# Revit family: Kessel 27611 en
name_source: partatom
category: Pipe Accessories
revit_build: Autodesk Revit Architecture 2014 (Build: 20130308_1515(x64)
units: mm (PartAtom-declared; Revit-internal decimal feet)

## types (1)
- Kessel 27611 en
    <1.010.00.2> Number of the part of the guideline = 38
    <1.010.00.3> Issue date (month) of the guideline = 201805
    <1.010.00.4> Manufacturer name = Kessel
    <1.010.00.5> Revision date of the file = 20190228
    <1.800.00.3> BS number = 10001100000000000000000000000300000010000100000001???00001
    <1.800.00.4> Comment field = The Universal basement drain DN 100, black grating, backwater protection
    <1.810.00.3> Manufacturer’s reference number = 27611
    <1.810.00.4> DATANORM number = 27611
    <1.810.00.6> GTIN number = 4026092007822
    <1.960/3L.00.8> Link (URL) = http://www.kessel.de
    <38.100.00.4> Drain type for floor, roof and sanitary objects = Backwater valves
    <38.110.00.4> Floor, roof and sanitary works sequences = The Universal basement drain
    <38.400.00.3> Material of the drain body = polymer
    <38.500.00.3> Sealing variantion = -
    <38.550.00.3> Trap = with odour trap
    <38.700.00.15> Connection to GLT, GA = no
    <38.700.00.16> Fire resistance class can be retrofitted = no
    <38.700.00.18> Load class Drains, covers and attachments = K 3
    <38.700.00.4> product name = The Universal basement drain DN 100, black grating, backwater protection
    <38.700.00.6> Complete article (one-piece) from combination (multi-part design) Drain body and attachment piece = yes
    <38.700.00.7> Potential compensation (ground connection) available = no
    <38.700.00.8> Electrical connection = no
    <38.710.01.10> depth [mm] = 300
    <38.710.01.14> with sound decoupling = no
    <38.710.01.15> Leafy / Kiefang = no
    <38.710.01.3> Product name = The Universal basement drain DN 100, black grating, backwater protection
    <38.710.01.4> Type = floor drain
    <38.710.01.5> Nominal system = DN
    <38.710.01.6> Nominal dimensions = 100
    <38.710.01.9> installation width [mm] = 380
    <38.710.11.3> drainage capacity [l/s] = 1.8
    <38.710.13.3> Product name = The Universal basement drain DN 100, black grating, backwater protection
    <38.710.13.4> Variant of the drainage drain = point drain
    <38.710.13.7> Leafy / Kiefang = no
    <38.710.15.10> Load class Drains, covers and attachments = K 3
    <38.710.15.3> Product name = Slotted grating, plastic
    <38.710.15.4> Execution drain grate = Slotted cover
    <38.710.15.5> Material of the drain grate = plastic
    <38.710.15.7> Execution of the drain grate = Slotted cover
    <38.710.15.9> Slip resistance of the drain grate = no
    <38.710.16.3> Type of measurements = external dimensions
    <38.710.16.4> Length = 380
    <38.710.16.5> Width = 300
    <38.710.16.7> Mass (net) = 2.38
    CONNECTOR0_ref_dZ = 1 mm  [stored 0.00328084 ft]
    CONNECTOR1_DIAMETER_dY_0r = 0 mm  [stored 0 ft]
    CONNECTOR1_dY_00 = 143 mm
    CONNECTOR1_dY_01 = 133 mm
    CONNECTOR1_ref_dY = 133 mm
    CONNECTOR1_ref_dZ = 130 mm
    CONNECTOR2_DIAMETER_dY_0r = 0 mm  [stored 0 ft]
    CONNECTOR2_dY_00 = 133 mm
    CONNECTOR2_dY_01 = 143 mm
    CONNECTOR2_ref_dY = 133 mm
    CONNECTOR2_ref_dZ = 130 mm
    CONNECTOR3_DIAMETER_dX_0r = 0 mm  [stored 0 ft]
    CONNECTOR3_dX_00 = 176 mm
    CONNECTOR3_dX_01 = 166 mm
    CONNECTOR3_ref_dX = 166 mm
    CONNECTOR3_ref_dZ = 121 mm
    CONNECTOR4_DIAMETER_dX_0r = 0 mm  [stored 0 ft]
    CONNECTOR4_dX_00 = 188 mm
    CONNECTOR4_dX_01 = 198 mm
    CONNECTOR4_ref_dX = 188 mm
    CONNECTOR4_ref_dZ = 121 mm
    Manufacturer = Kessel
    Model = 27611
    URL = www.kessel.com

note: [stored X ft] marks values corroborated as IEEE doubles in the binary element streams (Revit-internal decimal feet)
